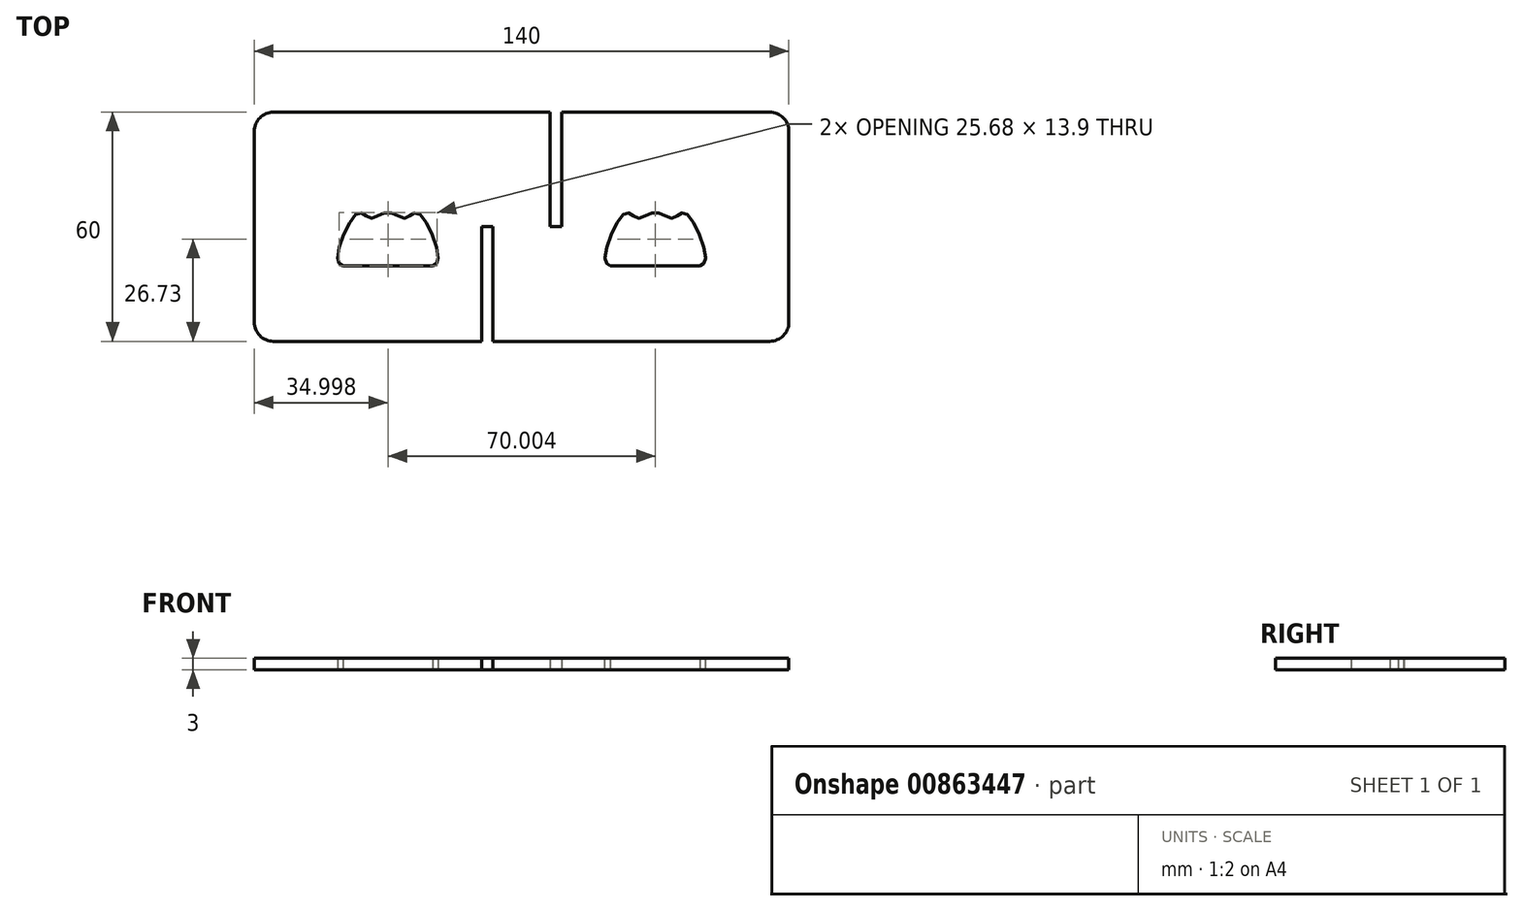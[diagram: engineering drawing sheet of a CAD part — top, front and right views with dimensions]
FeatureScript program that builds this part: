
annotation { "Feature Type Name" : "Feature", "Feature Type Description" : "" }
export const myFeature = defineFeature(function(context is Context, id is Id, definition is map)
    precondition{}
    {
        {
            var Q0;
            Q0=qCreatedBy(makeId("Top.planeOp"),FACE);
            var sketch = newSketch(context, id + "F0", { "sketchPlane" : qUnion([Q0])});
            skLineSegment(sketch, "E0.bottom", {"start": v(-70, -30) * mm, "end": v(-10.5, -30) * mm});
            skLineSegment(sketch, "E0.top", {"start": v(-70, 30) * mm, "end": v(7.5, 30) * mm});
            skLineSegment(sketch, "E0.left", {"start": v(-70, -30) * mm, "end": v(-70, 30) * mm});
            skLineSegment(sketch, "E0.right", {"start": v(70, -30) * mm, "end": v(70, 30) * mm});
            skPoint(sketch, "E0.middle", {"position": v(0, 0) * mm});
            skLineSegment(sketch, "E1.bottom", {"start": v(7.5, 25) * mm, "end": v(7.5, 25) * mm});
            skLineSegment(sketch, "E2", {"start": v(7.5, 25) * mm, "end": v(7.5, 0) * mm});
            skLineSegment(sketch, "E3", {"start": v(10.5, 25) * mm, "end": v(10.5, 0) * mm});
            skPoint(sketch, "E4", {"position": v(-35, -10.22) * mm});
            skLineSegment(sketch, "E5", {"start": v(-35, -10.22) * mm, "end": v(-46.75, -10.22) * mm});
            skLineSegment(sketch, "E6", {"start": v(-35, -10.22) * mm, "end": v(-23.25, -10.22) * mm});
            skPoint(sketch, "E7", {"position": v(-35, -3.27) * mm});
            skPoint(sketch, "E8", {"position": v(-35, 3.68) * mm});
            skPoint(sketch, "E9", {"position": v(-39.7, 2.28) * mm});
            skPoint(sketch, "E10", {"position": v(-30.3, 2.28) * mm});
            skPoint(sketch, "E11", {"position": v(-42.7, 3.68) * mm});
            skPoint(sketch, "E12", {"position": v(-27.3, 3.68) * mm});
            skPoint(sketch, "E13", {"position": v(-48.18, -8.3) * mm});
            skPoint(sketch, "E14", {"position": v(-46.75, -10.22) * mm});
            skPoint(sketch, "E15", {"position": v(-23.25, -10.22) * mm});
            skPoint(sketch, "E16", {"position": v(-21.82, -8.29) * mm});
            skFitSpline(sketch, "E17", {"points": [v(-46.75, -10.22) * mm, v(-48.18, -8.3) * mm, v(-42.7, 3.68) * mm, v(-39.7, 2.28) * mm, v(-35, 3.68) * mm, v(-30.3, 2.28) * mm, v(-27.3, 3.68) * mm, v(-21.82, -8.29) * mm, v(-23.25, -10.22) * mm], "startDerivative": vector(-24.65, 11.44) * mm, "endDerivative": vector(-24.55, -11.6) * mm});
            skPoint(sketch, "E18.MirrorP", {"position": v(35, 3.68) * mm});
            skPoint(sketch, "E19.MirrorP", {"position": v(27.3, 3.68) * mm});
            skPoint(sketch, "E20.MirrorP", {"position": v(23.25, -10.22) * mm});
            skPoint(sketch, "E21.MirrorP", {"position": v(35, -3.27) * mm});
            skPoint(sketch, "E22.MirrorP", {"position": v(21.82, -8.29) * mm});
            skFitSpline(sketch, "E23.MirrorCS", {"points": [v(46.75, -10.22) * mm, v(48.18, -8.3) * mm, v(42.7, 3.68) * mm, v(39.7, 2.28) * mm, v(35, 3.68) * mm, v(30.3, 2.28) * mm, v(27.3, 3.68) * mm, v(21.82, -8.29) * mm, v(23.25, -10.22) * mm], "startDerivative": vector(24.65, 11.44) * mm, "endDerivative": vector(24.55, -11.6) * mm});
            skLineSegment(sketch, "E24.MirrorCS", {"start": v(35, -10.22) * mm, "end": v(23.25, -10.22) * mm});
            skLineSegment(sketch, "E25.MirrorCS", {"start": v(35, -10.22) * mm, "end": v(46.75, -10.22) * mm});
            skPoint(sketch, "E26.MirrorP", {"position": v(35, -10.22) * mm});
            skLineSegment(sketch, "E27", {"start": v(7.5, 25) * mm, "end": v(7.5, 30) * mm});
            skLineSegment(sketch, "E28", {"start": v(10.5, 25) * mm, "end": v(10.5, 30) * mm});
            skLineSegment(sketch, "E29", {"start": v(-10.5, 0) * mm, "end": v(-7.5, 0) * mm});
            skLineSegment(sketch, "E30", {"start": v(7.5, 0) * mm, "end": v(10.5, 0) * mm});
            skLineSegment(sketch, "E31", {"start": v(-10.5, 0) * mm, "end": v(-10.5, -30) * mm});
            skLineSegment(sketch, "E32", {"start": v(-7.5, 0) * mm, "end": v(-7.5, -30) * mm});
            skLineSegment(sketch, "E33.trimOffspring", {"start": v(-7.5, -30) * mm, "end": v(70, -30) * mm});
            skLineSegment(sketch, "E34.trimOffspring", {"start": v(10.5, 30) * mm, "end": v(70, 30) * mm});
            skSolve(sketch);
        }
        {
            var Q0;
            Q0=makeQuery(id+"F0.imprint","IMPRINT",FACE,{"disambiguationData":[TD([[makeQuery(id+"F0.imprint","IMPRINT",EDGE,{"derivedFrom":sQuery(id+"F0.wireOp",EDGE,"E0.bottom")}),1.0]])]});
            extrude(context, id + "F1", {"entities" : qUnion([Q0]), "depth" : 3 * mm, "offsetDistance" : 25 * mm});
        }
        {
            var Q0;
            Q0=makeQuery(id+"F1.opExtrude","SWEPT_EDGE",EDGE,{"disambiguationData":[OSD([sQuery(id+"F0.wireOp",EDGE,"E0.right"),sQuery(id+"F0.wireOp",EDGE,"E33.trimOffspring")])]});
            var Q1;
            Q1=makeQuery(id+"F1.opExtrude","SWEPT_EDGE",EDGE,{"disambiguationData":[OSD([sQuery(id+"F0.wireOp",EDGE,"E0.right"),sQuery(id+"F0.wireOp",EDGE,"E34.trimOffspring")])]});
            var Q2;
            Q2=makeQuery(id+"F1.opExtrude","SWEPT_EDGE",EDGE,{"disambiguationData":[OSD([sQuery(id+"F0.wireOp",EDGE,"E0.top"),sQuery(id+"F0.wireOp",EDGE,"E0.left")])]});
            var Q3;
            Q3=makeQuery(id+"F1.opExtrude","SWEPT_EDGE",EDGE,{"disambiguationData":[OSD([sQuery(id+"F0.wireOp",EDGE,"E0.bottom"),sQuery(id+"F0.wireOp",EDGE,"E0.left")])]});
            fillet(context, id + "F2", {"entities" : qUnion([Q0, Q1, Q2, Q3]), "radius" : 5 * mm, "tangentPropagation" : true, "allowEdgeOverflow" : false});
        }
    });
